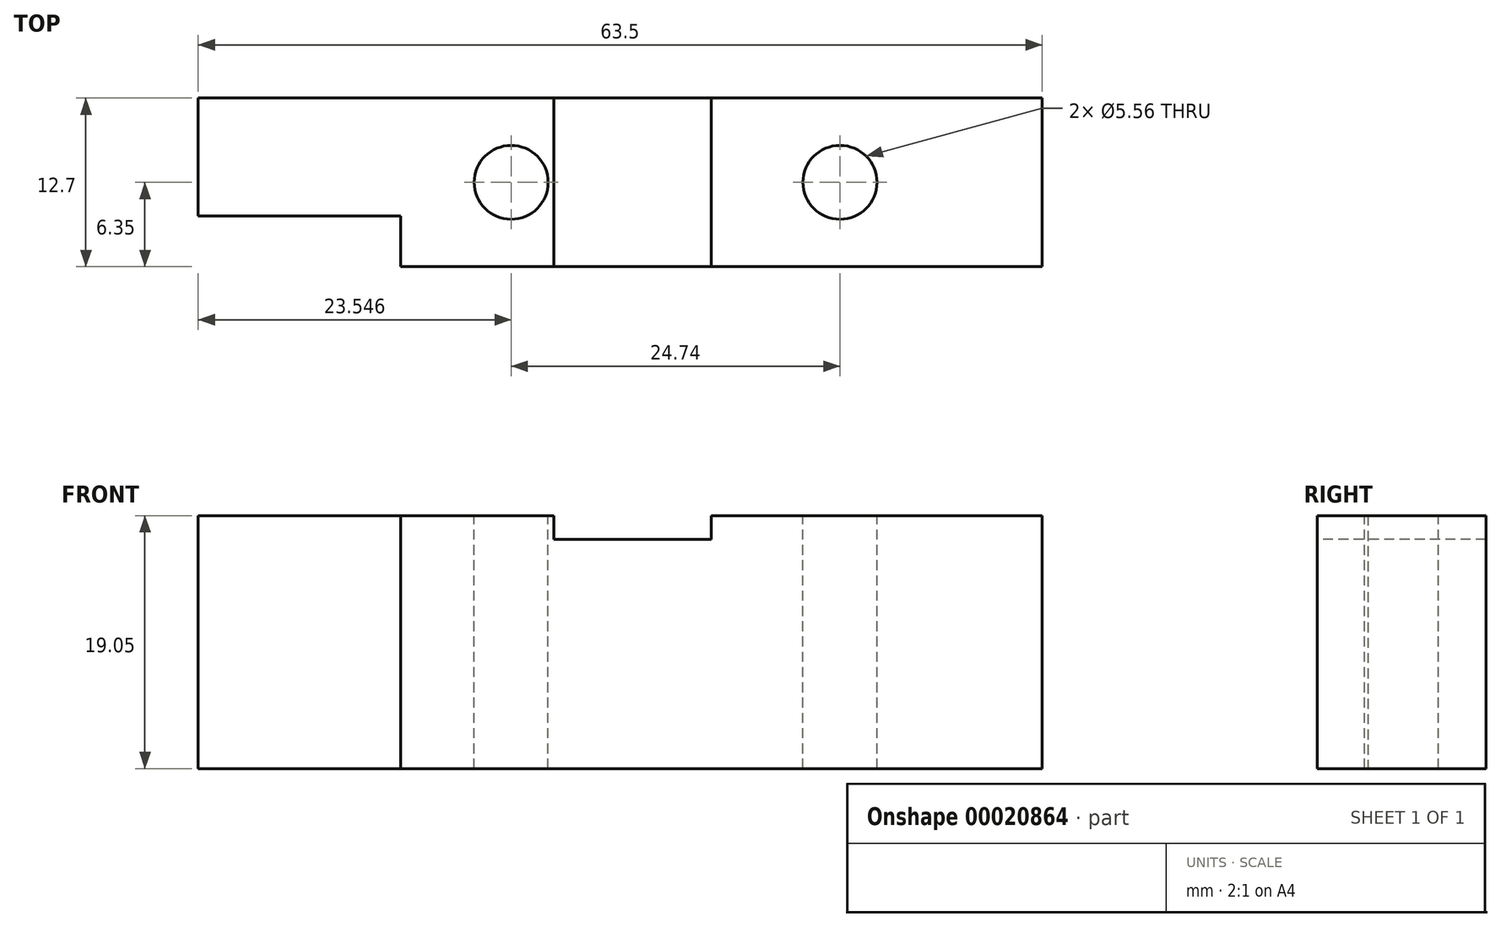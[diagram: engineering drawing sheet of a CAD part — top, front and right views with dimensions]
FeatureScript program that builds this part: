
annotation { "Feature Type Name" : "Feature", "Feature Type Description" : "" }
export const myFeature = defineFeature(function(context is Context, id is Id, definition is map)
    precondition{}
    {
        {
            var Q0;
            Q0=qCreatedBy(makeId("Top.planeOp"),FACE);
            var sketch = newSketch(context, id + "F0", { "sketchPlane" : qUnion([Q0])});
            skLineSegment(sketch, "E0.bottom", {"start": v(0, 0) * mm, "end": v(63.5, 0) * mm});
            skLineSegment(sketch, "E0.top", {"start": v(0, -12.7) * mm, "end": v(63.5, -12.7) * mm});
            skLineSegment(sketch, "E0.left", {"start": v(0, 0) * mm, "end": v(0, -12.7) * mm});
            skLineSegment(sketch, "E0.right", {"start": v(63.5, 0) * mm, "end": v(63.5, -12.7) * mm});
            skSolve(sketch);
        }
        {
            var Q0;
            Q0=makeQuery(id+"F0.imprint","IMPRINT",FACE,{"disambiguationData":[TD([[makeQuery(id+"F0.imprint","IMPRINT",EDGE,{"derivedFrom":sQuery(id+"F0.wireOp",EDGE,"E0.bottom")}),-1.0]])]});
            extrude(context, id + "F1", {"entities" : qUnion([Q0]), "depth" : 19.05 * mm});
        }
        {
            var Q0;
            Q0=makeQuery(id+"F1.opExtrude","SWEPT_FACE",FACE,{"disambiguationData":[OSD([sQuery(id+"F0.wireOp",EDGE,"E0.top")])]});
            var sketch = newSketch(context, id + "F2", { "sketchPlane" : qUnion([Q0])});
            skLineSegment(sketch, "E1.bottom", {"start": v(26.75, 19.05) * mm, "end": v(38.6, 19.05) * mm});
            skLineSegment(sketch, "E1.top", {"start": v(26.75, 17.27) * mm, "end": v(38.6, 17.27) * mm});
            skLineSegment(sketch, "E1.left", {"start": v(26.75, 19.05) * mm, "end": v(26.75, 17.27) * mm});
            skLineSegment(sketch, "E1.right", {"start": v(38.6, 19.05) * mm, "end": v(38.6, 17.27) * mm});
            skSolve(sketch);
        }
        {
            var Q0;
            Q0=makeQuery(id+"F2.imprint","IMPRINT",FACE,{"disambiguationData":[TD([[makeQuery(id+"F2.imprint","IMPRINT",EDGE,{"derivedFrom":sQuery(id+"F2.wireOp",EDGE,"E1.bottom")}),-1.0]])]});
            extrude(context, id + "F3", {"entities" : qUnion([Q0]), "operationType" : NewBodyOperationType.REMOVE, "endBound" : BoundingType.THROUGH_ALL, "oppositeDirection" : true, "depth" : 25.4 * mm});
        }
        {
            var Q0;
            {var subQ0=sQuery(id+"F0.wireOp",EDGE,"E0.bottom");var subQ1=sQuery(id+"F0.wireOp",EDGE,"E0.top");var subQ2=sQuery(id+"F0.wireOp",EDGE,"E0.right");Q0=makeQuery(id+"F3.boolean.opBoolean","SPLIT",FACE,{"disambiguationData":[TD([makeQuery(id+"F1.opExtrude","SWEPT_FACE",FACE,{"disambiguationData":[OSD([subQ2])]})])],"derivedFrom":makeQuery(id+"F1.opExtrude","CAP_FACE",FACE,{"disambiguationData":[OSD([subQ0,subQ1,sQuery(id+"F0.wireOp",EDGE,"E0.left"),subQ2])],"isStart":false})});}
            var sketch = newSketch(context, id + "F4", { "sketchPlane" : qUnion([Q0])});
            skCircle(sketch, "E2", {"center": v(48.29, -6.35) * mm, "radius": 2.78 * mm});
            skSolve(sketch);
        }
        {
            var Q0;
            Q0=makeQuery(id+"F4.imprint","IMPRINT",FACE,{"disambiguationData":[TD([[makeQuery(id+"F4.imprint","IMPRINT",EDGE,{"derivedFrom":sQuery(id+"F4.wireOp",EDGE,"E2")}),1.0]])]});
            extrude(context, id + "F5", {"entities" : qUnion([Q0]), "operationType" : NewBodyOperationType.REMOVE, "oppositeDirection" : true, "depth" : 25.4 * mm});
        }
        {
            var Q0;
            {var subQ0=sQuery(id+"F0.wireOp",EDGE,"E0.bottom");var subQ1=sQuery(id+"F0.wireOp",EDGE,"E0.top");var subQ2=sQuery(id+"F0.wireOp",EDGE,"E0.left");Q0=makeQuery(id+"F3.boolean.opBoolean","SPLIT",FACE,{"disambiguationData":[TD([makeQuery(id+"F1.opExtrude","SWEPT_FACE",FACE,{"disambiguationData":[OSD([subQ2])]})])],"derivedFrom":makeQuery(id+"F1.opExtrude","CAP_FACE",FACE,{"disambiguationData":[OSD([subQ0,subQ1,subQ2,sQuery(id+"F0.wireOp",EDGE,"E0.right")])],"isStart":false})});}
            var sketch = newSketch(context, id + "F6", { "sketchPlane" : qUnion([Q0])});
            skCircle(sketch, "E3", {"center": v(23.55, -6.35) * mm, "radius": 2.78 * mm});
            skSolve(sketch);
        }
        {
            var Q0;
            Q0=makeQuery(id+"F6.imprint","IMPRINT",FACE,{"disambiguationData":[TD([[makeQuery(id+"F6.imprint","IMPRINT",EDGE,{"derivedFrom":sQuery(id+"F6.wireOp",EDGE,"E3")}),1.0]])]});
            extrude(context, id + "F7", {"entities" : qUnion([Q0]), "operationType" : NewBodyOperationType.REMOVE, "endBound" : BoundingType.THROUGH_ALL, "oppositeDirection" : true, "depth" : 25.4 * mm});
        }
        {
            var Q0;
            Q0=makeQuery(id+"F1.opExtrude","CAP_FACE",FACE,{"disambiguationData":[OSD([sQuery(id+"F0.wireOp",EDGE,"E0.bottom"),sQuery(id+"F0.wireOp",EDGE,"E0.top"),sQuery(id+"F0.wireOp",EDGE,"E0.left"),sQuery(id+"F0.wireOp",EDGE,"E0.right")])],"isStart":true});
            var sketch = newSketch(context, id + "F8", { "sketchPlane" : qUnion([Q0])});
            skLineSegment(sketch, "E4.bottom", {"start": v(0, 12.7) * mm, "end": v(15.24, 12.7) * mm});
            skLineSegment(sketch, "E4.top", {"start": v(0, 8.9) * mm, "end": v(15.24, 8.9) * mm});
            skLineSegment(sketch, "E4.left", {"start": v(0, 12.7) * mm, "end": v(0, 8.9) * mm});
            skLineSegment(sketch, "E4.right", {"start": v(15.24, 12.7) * mm, "end": v(15.24, 8.89) * mm});
            skSolve(sketch);
        }
        {
            var Q0;
            Q0=makeQuery(id+"F8.imprint","IMPRINT",FACE,{"disambiguationData":[TD([[makeQuery(id+"F8.imprint","IMPRINT",EDGE,{"derivedFrom":sQuery(id+"F8.wireOp",EDGE,"E4.bottom")}),-1.0]])]});
            extrude(context, id + "F9", {"entities" : qUnion([Q0]), "operationType" : NewBodyOperationType.REMOVE, "endBound" : BoundingType.THROUGH_ALL, "oppositeDirection" : true, "depth" : 25.4 * mm});
        }
    });
